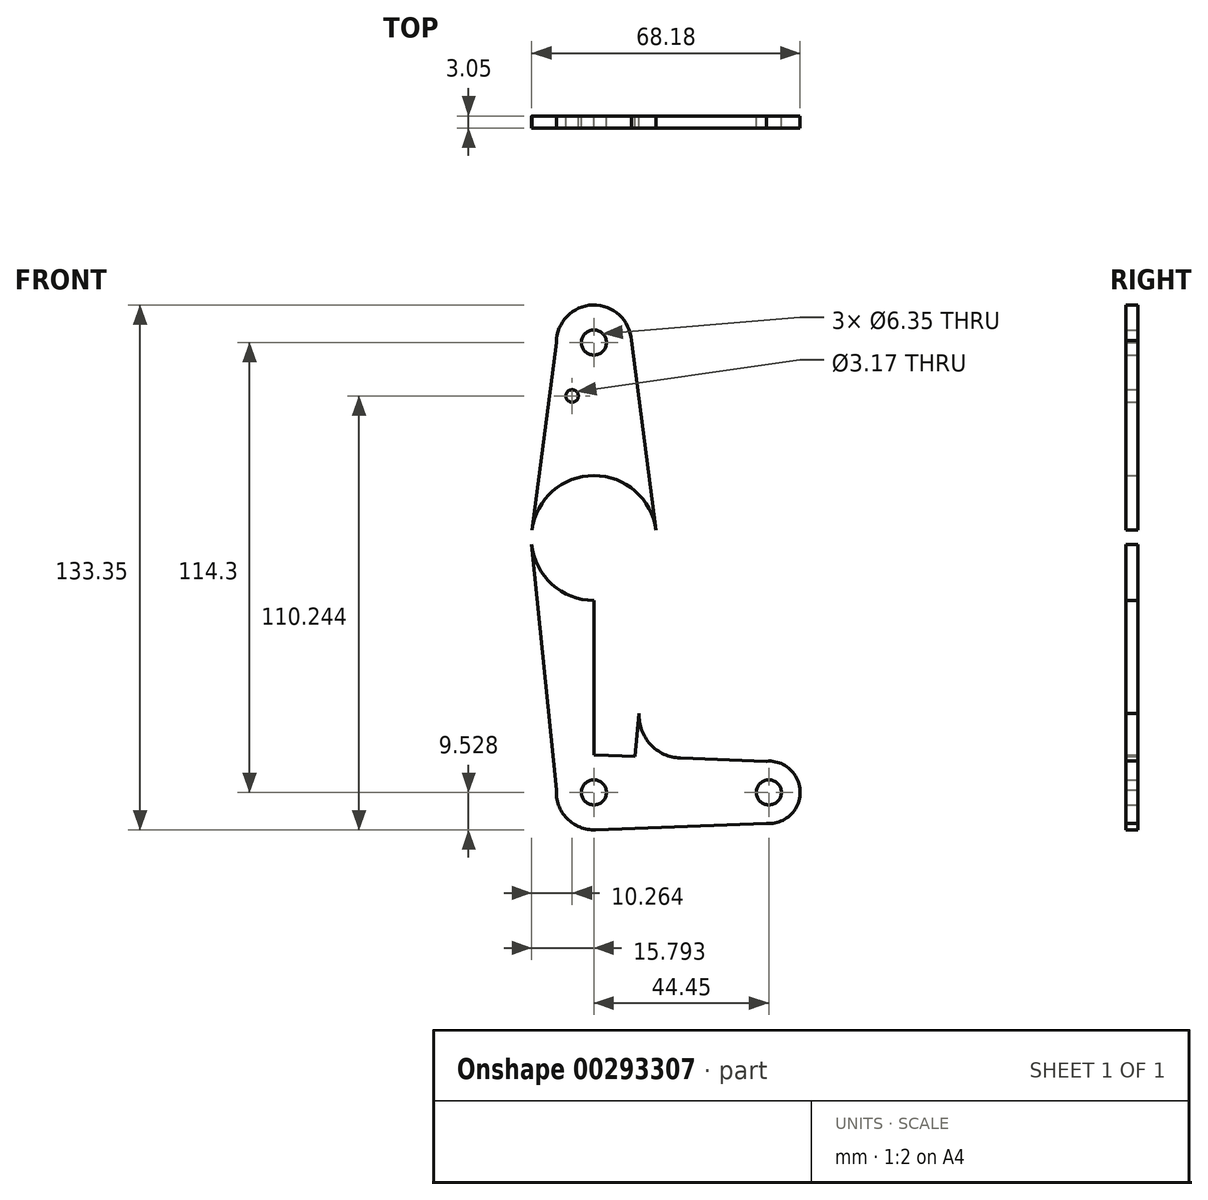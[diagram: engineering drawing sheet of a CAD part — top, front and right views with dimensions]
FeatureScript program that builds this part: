
annotation { "Feature Type Name" : "Feature", "Feature Type Description" : "" }
export const myFeature = defineFeature(function(context is Context, id is Id, definition is map)
    precondition{}
    {
        {
            var Q0;
            Q0=qCreatedBy(makeId("Front.planeOp"),FACE);
            var sketch = newSketch(context, id + "F0", { "sketchPlane" : qUnion([Q0])});
            skLineSegment(sketch, "E0", {"start": v(-47.4, 60.05) * mm, "end": v(-47.4, -54.25) * mm});
            skLineSegment(sketch, "E1", {"start": v(-47.4, -54.25) * mm, "end": v(-2.96, -54.25) * mm});
            skCircle(sketch, "E2", {"center": v(-47.4, 60.05) * mm, "radius": 9.53 * mm});
            skCircle(sketch, "E3", {"center": v(-47.4, 10.36) * mm, "radius": 15.88 * mm});
            skCircle(sketch, "E4", {"center": v(-47.4, -54.25) * mm, "radius": 9.53 * mm});
            skCircle(sketch, "E5", {"center": v(-2.96, -54.25) * mm, "radius": 7.94 * mm});
            skLineSegment(sketch, "E6", {"start": v(-56.93, 60.05) * mm, "end": v(-63.15, 12.42) * mm});
            skLineSegment(sketch, "E7", {"start": v(-37.9, 60.55) * mm, "end": v(-31.66, 12.4) * mm});
            skLineSegment(sketch, "E8", {"start": v(-56.9, -53.6) * mm, "end": v(-63.2, 8.77) * mm});
            skLineSegment(sketch, "E9", {"start": v(-37.88, -54.25) * mm, "end": v(-31.61, 8.77) * mm});
            skPoint(sketch, "E9.startSnap0", {"position": v(-25.18, -54.25) * mm});
            skLineSegment(sketch, "E10", {"start": v(-3.53, -46.34) * mm, "end": v(-47.4, -44.72) * mm});
            skLineSegment(sketch, "E11", {"start": v(-3.57, -62.17) * mm, "end": v(-47.06, -63.77) * mm});
            skCircle(sketch, "E12", {"center": v(-47.4, 60.05) * mm, "radius": 3.18 * mm});
            skCircle(sketch, "E13", {"center": v(-52.94, 46.46) * mm, "radius": 1.59 * mm});
            skCircle(sketch, "E14", {"center": v(-47.4, 10.36) * mm, "radius": 3.18 * mm});
            skCircle(sketch, "E15", {"center": v(-47.4, -54.25) * mm, "radius": 3.18 * mm});
            skCircle(sketch, "E16", {"center": v(-2.96, -54.25) * mm, "radius": 3.18 * mm});
            skArc(sketch, "E17", {"start": v(-35.9, -34.24) * mm, "mid": v(-33.05, -42.07) * mm, "end": v(-25.47, -45.53) * mm});
            skSolve(sketch);
        }
        {
            var Q0;
            {var subQ0=sQuery(id+"F0.wireOp",EDGE,"E17");var subQ1=sQuery(id+"F0.wireOp",EDGE,"E10");var subQ2=makeQuery(id+"F0.imprint","INTERSECT",VERTEX,{"disambiguationData":[OD(0.0)],"derivedFrom":[subQ1,subQ0]});Q0=makeQuery(id+"F0.imprint","IMPRINT",FACE,{"disambiguationData":[TD([[makeQuery(id+"F0.imprint","IMPRINT",EDGE,{"disambiguationData":[TD([[subQ2,-1.0]])],"derivedFrom":subQ1}),1.0]])]});}
            var Q1;
            {var subQ0=sQuery(id+"F0.wireOp",EDGE,"E17");var subQ1=sQuery(id+"F0.wireOp",EDGE,"E9");var subQ2=makeQuery(id+"F0.imprint","INTERSECT",VERTEX,{"derivedFrom":[subQ1,subQ0]});Q1=makeQuery(id+"F0.imprint","IMPRINT",FACE,{"disambiguationData":[TD([[makeQuery(id+"F0.imprint","IMPRINT",EDGE,{"disambiguationData":[TD([[subQ2,1.0]])],"derivedFrom":subQ1}),-1.0]])]});}
            var Q2;
            {var subQ5=sQuery(id+"F0.wireOp",EDGE,"E7");Q2=makeQuery(id+"F0.imprint","IMPRINT",FACE,{"disambiguationData":[TD([[makeQuery(id+"F0.imprint","IMPRINT",EDGE,{"derivedFrom":subQ5}),-1.0]])]});}
            var Q3;
            {var subQ5=sQuery(id+"F0.wireOp",EDGE,"E11");Q3=makeQuery(id+"F0.imprint","IMPRINT",FACE,{"disambiguationData":[TD([[makeQuery(id+"F0.imprint","IMPRINT",EDGE,{"derivedFrom":subQ5}),-1.0]])]});}
            var Q4;
            Q4=makeQuery(id+"F0.imprint","IMPRINT",FACE,{"disambiguationData":[TD([[makeQuery(id+"F0.imprint","IMPRINT",EDGE,{"derivedFrom":sQuery(id+"F0.wireOp",EDGE,"E12")}),-1.0]])]});
            var Q5;
            Q5=makeQuery(id+"F0.imprint","IMPRINT",FACE,{"disambiguationData":[TD([[makeQuery(id+"F0.imprint","IMPRINT",EDGE,{"derivedFrom":sQuery(id+"F0.wireOp",EDGE,"E16")}),-1.0]])]});
            var Q6;
            {var subQ0=sQuery(id+"F0.wireOp",EDGE,"E6");Q6=makeQuery(id+"F0.imprint","IMPRINT",FACE,{"disambiguationData":[TD([[makeQuery(id+"F0.imprint","IMPRINT",EDGE,{"derivedFrom":subQ0}),1.0]])]});}
            var Q7;
            {var subQ0=sQuery(id+"F0.wireOp",EDGE,"E3");var subQ2=sQuery(id+"F0.wireOp",EDGE,"E0");var subQ3=makeQuery(id+"F0.imprint","INTERSECT",VERTEX,{"disambiguationData":[OD(0.0)],"derivedFrom":[subQ2,subQ0]});Q7=makeQuery(id+"F0.imprint","IMPRINT",FACE,{"disambiguationData":[TD([[makeQuery(id+"F0.imprint","IMPRINT",EDGE,{"disambiguationData":[TD([[subQ3,-1.0]])],"derivedFrom":subQ2}),1.0]])]});}
            var Q8;
            {var subQ0=sQuery(id+"F0.wireOp",EDGE,"E3");var subQ2=sQuery(id+"F0.wireOp",EDGE,"E0");var subQ3=makeQuery(id+"F0.imprint","INTERSECT",VERTEX,{"disambiguationData":[OD(0.0)],"derivedFrom":[subQ2,subQ0]});Q8=makeQuery(id+"F0.imprint","IMPRINT",FACE,{"disambiguationData":[TD([[makeQuery(id+"F0.imprint","IMPRINT",EDGE,{"disambiguationData":[TD([[subQ3,-1.0]])],"derivedFrom":subQ2}),-1.0]])]});}
            var Q9;
            {var subQ0=sQuery(id+"F0.wireOp",EDGE,"E8");Q9=makeQuery(id+"F0.imprint","IMPRINT",FACE,{"disambiguationData":[TD([[makeQuery(id+"F0.imprint","IMPRINT",EDGE,{"derivedFrom":subQ0}),-1.0]])]});}
            var Q10;
            {var subQ0=sQuery(id+"F0.wireOp",EDGE,"E4");var subQ4=sQuery(id+"F0.wireOp",EDGE,"E0");var subQ8=makeQuery(id+"F0.imprint","INTERSECT",VERTEX,{"derivedFrom":[subQ4,subQ0]});Q10=makeQuery(id+"F0.imprint","IMPRINT",FACE,{"disambiguationData":[TD([[makeQuery(id+"F0.imprint","IMPRINT",EDGE,{"disambiguationData":[TD([[subQ8,-1.0]])],"derivedFrom":subQ4}),-1.0]])]});}
            var Q11;
            {var subQ0=sQuery(id+"F0.wireOp",EDGE,"E10");var subQ1=sQuery(id+"F0.wireOp",EDGE,"E5");var subQ2=makeQuery(id+"F0.imprint","INTERSECT",VERTEX,{"derivedFrom":[subQ1,subQ0]});Q11=makeQuery(id+"F0.imprint","IMPRINT",FACE,{"disambiguationData":[TD([[makeQuery(id+"F0.imprint","IMPRINT",EDGE,{"disambiguationData":[TD([[subQ2,-1.0]])],"derivedFrom":subQ1}),-1.0]])]});}
            var Q12;
            {var subQ2=sQuery(id+"F0.wireOp",EDGE,"E10");var subQ6=sQuery(id+"F0.wireOp",EDGE,"E0");var subQ8=makeQuery(id+"F0.imprint","INTERSECT",VERTEX,{"derivedFrom":[subQ6,subQ2]});Q12=makeQuery(id+"F0.imprint","IMPRINT",FACE,{"disambiguationData":[TD([[makeQuery(id+"F0.imprint","IMPRINT",EDGE,{"disambiguationData":[TD([[subQ8,1.0]])],"derivedFrom":subQ6}),1.0]])]});}
            var Q13;
            {var subQ0=sQuery(id+"F0.wireOp",EDGE,"E4");var subQ6=sQuery(id+"F0.wireOp",EDGE,"E0");var subQ7=makeQuery(id+"F0.imprint","INTERSECT",VERTEX,{"derivedFrom":[subQ6,subQ0]});Q13=makeQuery(id+"F0.imprint","IMPRINT",FACE,{"disambiguationData":[TD([[makeQuery(id+"F0.imprint","IMPRINT",EDGE,{"disambiguationData":[TD([[subQ7,-1.0]])],"derivedFrom":subQ6}),1.0]])]});}
            var Q14;
            {var subQ1=sQuery(id+"F0.wireOp",EDGE,"E4");var subQ3=sQuery(id+"F0.wireOp",EDGE,"E10");var subQ4=makeQuery(id+"F0.imprint","INTERSECT",VERTEX,{"derivedFrom":[subQ1,subQ3]});Q14=makeQuery(id+"F0.imprint","IMPRINT",FACE,{"disambiguationData":[TD([[makeQuery(id+"F0.imprint","IMPRINT",EDGE,{"disambiguationData":[TD([[subQ4,1.0]])],"derivedFrom":subQ3}),1.0]])]});}
            extrude(context, id + "F1", {"entities" : qUnion([Q0, Q1, Q2, Q3, Q4, Q5, Q6, Q7, Q8, Q9, Q10, Q11, Q12, Q13, Q14]), "depth" : 3.05 * mm});
        }
    });
